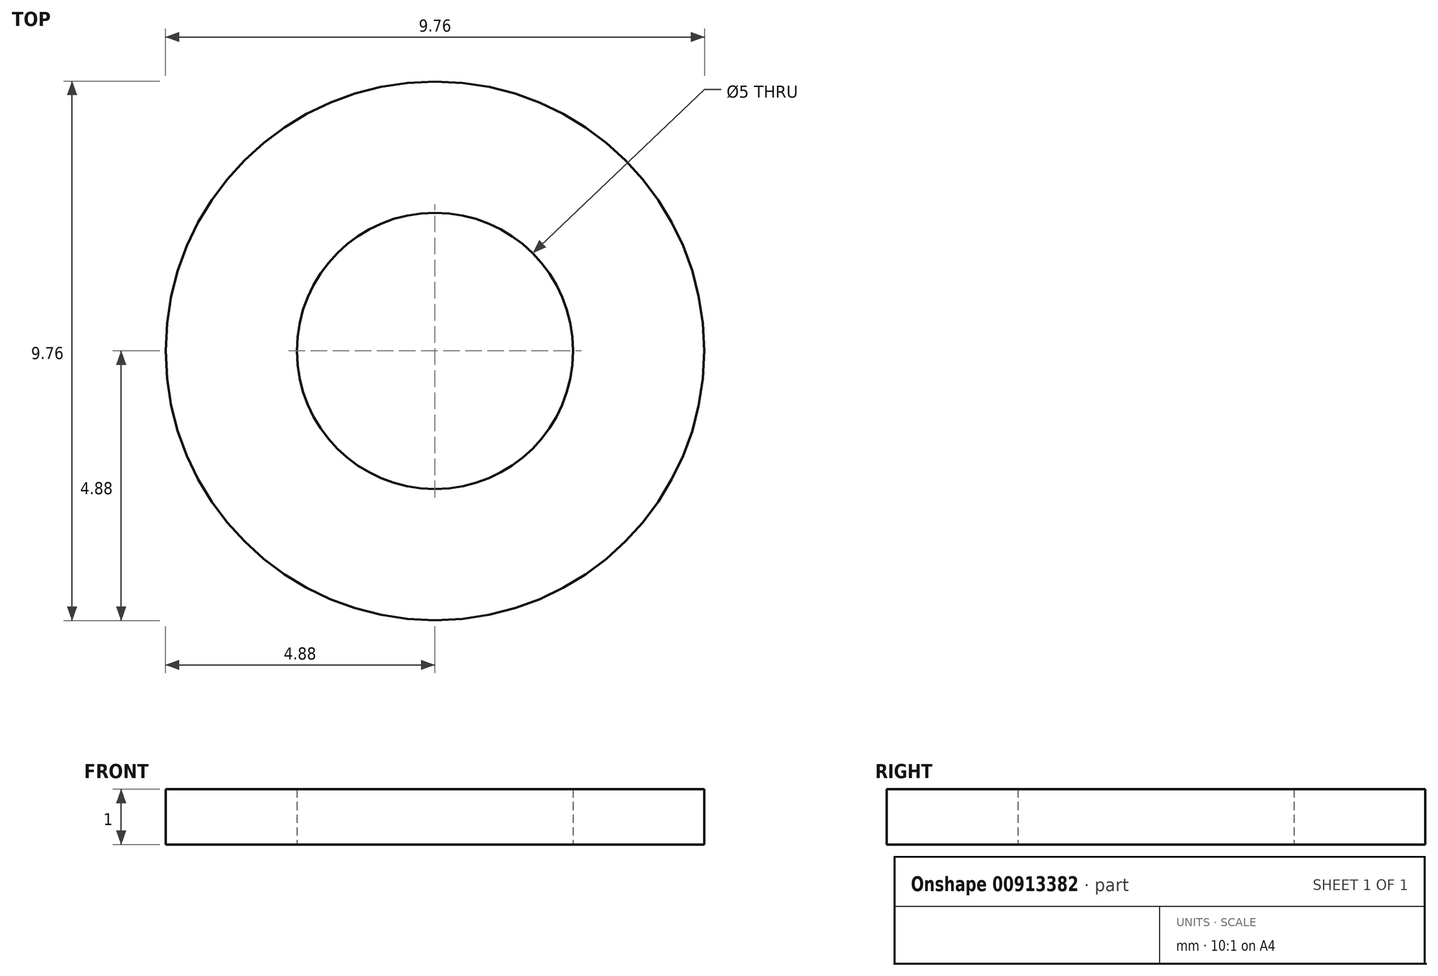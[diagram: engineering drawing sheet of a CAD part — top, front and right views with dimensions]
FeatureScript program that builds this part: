
annotation { "Feature Type Name" : "Feature", "Feature Type Description" : "" }
export const myFeature = defineFeature(function(context is Context, id is Id, definition is map)
    precondition{}
    {
        {
            var Q0;
            Q0=qCreatedBy(makeId("Top.planeOp"),FACE);
            var sketch = newSketch(context, id + "F0", { "sketchPlane" : qUnion([Q0])});
            skCircle(sketch, "E0", {"center": v(0, 0) * mm, "radius": 2.5 * mm});
            skCircle(sketch, "E1", {"center": v(0, 0) * mm, "radius": 4.88 * mm});
            skSolve(sketch);
        }
        {
            var Q0;
            Q0=qSketchRegion(id+"F0",true);
            extrude(context, id + "F1", {"entities" : qUnion([Q0]), "depth" : 1 * mm, "offsetDistance" : 25 * mm});
        }
    });
